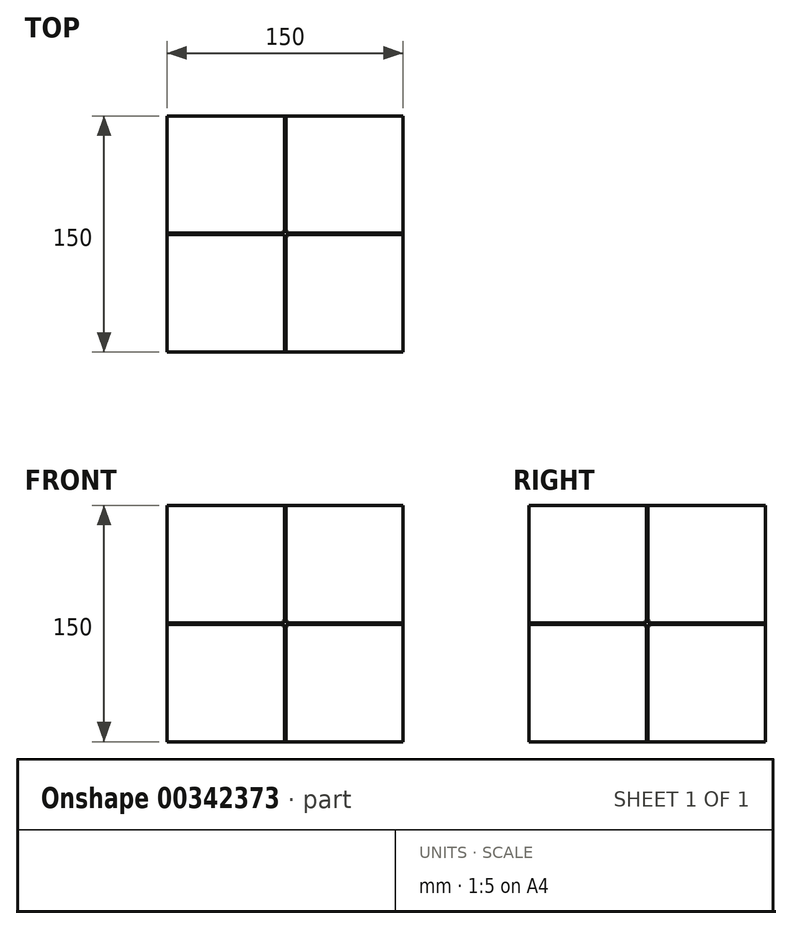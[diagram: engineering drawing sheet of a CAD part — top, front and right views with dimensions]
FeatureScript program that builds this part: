
annotation { "Feature Type Name" : "Feature", "Feature Type Description" : "" }
export const myFeature = defineFeature(function(context is Context, id is Id, definition is map)
    precondition{}
    {
        {
            var Q0;
            Q0=qCreatedBy(makeId("Front.planeOp"),FACE);
            var sketch = newSketch(context, id + "F0", { "sketchPlane" : qUnion([Q0])});
            skLineSegment(sketch, "E0.bottom", {"start": v(-75, 75) * mm, "end": v(75, 75) * mm});
            skLineSegment(sketch, "E0.top", {"start": v(-75, -75) * mm, "end": v(75, -75) * mm});
            skLineSegment(sketch, "E0.left", {"start": v(-75, 75) * mm, "end": v(-75, -75) * mm});
            skLineSegment(sketch, "E0.right", {"start": v(75, 75) * mm, "end": v(75, -75) * mm});
            skSolve(sketch);
        }
        {
            var Q0;
            Q0=makeQuery(id+"F0.imprint","IMPRINT",FACE,{"disambiguationData":[TD([[makeQuery(id+"F0.imprint","IMPRINT",EDGE,{"derivedFrom":sQuery(id+"F0.wireOp",EDGE,"E0.bottom")}),-1.0]])]});
            extrude(context, id + "F1", {"entities" : qUnion([Q0]), "endBound" : BoundingType.SYMMETRIC, "depth" : 1 * mm});
        }
        {
            var Q0;
            Q0=qCreatedBy(makeId("Top.planeOp"),FACE);
            var sketch = newSketch(context, id + "F2", { "sketchPlane" : qUnion([Q0])});
            skLineSegment(sketch, "E1.bottom", {"start": v(-75, 75) * mm, "end": v(75, 75) * mm});
            skLineSegment(sketch, "E1.top", {"start": v(-75, -75) * mm, "end": v(75, -75) * mm});
            skLineSegment(sketch, "E1.left", {"start": v(-75, 75) * mm, "end": v(-75, -75) * mm});
            skLineSegment(sketch, "E1.right", {"start": v(75, 75) * mm, "end": v(75, -75) * mm});
            skSolve(sketch);
        }
        {
            var Q0;
            Q0=makeQuery(id+"F2.imprint","IMPRINT",FACE,{"disambiguationData":[TD([[makeQuery(id+"F2.imprint","IMPRINT",EDGE,{"derivedFrom":sQuery(id+"F2.wireOp",EDGE,"E1.bottom")}),-1.0]])]});
            extrude(context, id + "F3", {"entities" : qUnion([Q0]), "operationType" : NewBodyOperationType.ADD, "endBound" : BoundingType.SYMMETRIC, "depth" : 1 * mm});
        }
        {
            var Q0;
            Q0=qCreatedBy(makeId("Right.planeOp"),FACE);
            var sketch = newSketch(context, id + "F4", { "sketchPlane" : qUnion([Q0])});
            skLineSegment(sketch, "E2.bottom", {"start": v(75, 75) * mm, "end": v(-75, 75) * mm});
            skLineSegment(sketch, "E2.top", {"start": v(75, -75) * mm, "end": v(-75, -75) * mm});
            skLineSegment(sketch, "E2.left", {"start": v(75, 75) * mm, "end": v(75, -75) * mm});
            skLineSegment(sketch, "E2.right", {"start": v(-75, 75) * mm, "end": v(-75, -75) * mm});
            skSolve(sketch);
        }
        {
            var Q0;
            Q0=makeQuery(id+"F4.imprint","IMPRINT",FACE,{"disambiguationData":[TD([[makeQuery(id+"F4.imprint","IMPRINT",EDGE,{"derivedFrom":sQuery(id+"F4.wireOp",EDGE,"E2.bottom")}),1.0]])]});
            extrude(context, id + "F5", {"entities" : qUnion([Q0]), "operationType" : NewBodyOperationType.ADD, "endBound" : BoundingType.SYMMETRIC, "depth" : 1 * mm});
        }
        {
            var Q0;
            Q0=qCreatedBy(makeId("Front.planeOp"),FACE);
            var sketch = newSketch(context, id + "F6", { "sketchPlane" : qUnion([Q0])});
            skArc(sketch, "E3", {"start": v(0, -2.5) * mm, "mid": v(2.5, 0) * mm, "end": v(0, 2.5) * mm});
            skLineSegment(sketch, "E4", {"start": v(0, 0) * mm, "end": v(0, 2.5) * mm});
            skLineSegment(sketch, "E5", {"start": v(0, 2.5) * mm, "end": v(0, -2.5) * mm});
            skSolve(sketch);
        }
        {
            var Q0;
            {var subQ0=sQuery(id+"F6.wireOp",EDGE,"E3");Q0=makeQuery(id+"F6.imprint","IMPRINT",FACE,{"disambiguationData":[TD([[makeQuery(id+"F6.imprint","IMPRINT",EDGE,{"derivedFrom":subQ0}),1.0]])]});}
            var Q1;
            Q1=sQuery(id+"F6.wireOp",EDGE,"E4");
            revolve(context, id + "F7", {"entities" : qUnion([Q0]), "axis" : qUnion([Q1]), "revolveType" : RevolveType.FULL});
        }
    });
